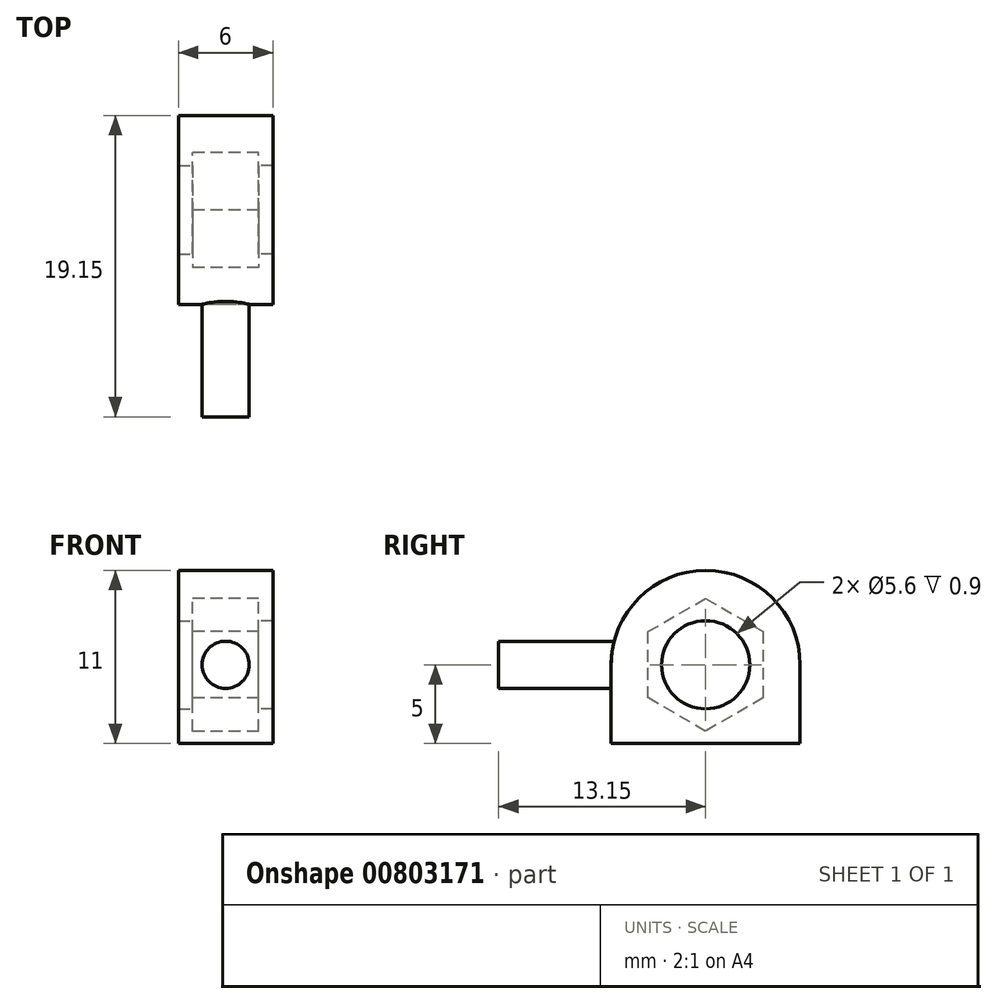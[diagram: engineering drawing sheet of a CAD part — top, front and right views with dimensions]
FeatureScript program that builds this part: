
annotation { "Feature Type Name" : "Feature", "Feature Type Description" : "" }
export const myFeature = defineFeature(function(context is Context, id is Id, definition is map)
    precondition{}
    {
        {
            var Q0;
            Q0=qCreatedBy(makeId("Right.planeOp"),FACE);
            var sketch = newSketch(context, id + "F0", { "sketchPlane" : qUnion([Q0])});
            skCircle(sketch, "E0.cCircle", {"center": v(0, 0) * mm, "radius": 3.65 * mm, "construction": true});
            skLineSegment(sketch, "E0.0", {"start": v(-3.65, 2.1) * mm, "end": v(0, 4.21) * mm});
            skLineSegment(sketch, "E0.1", {"start": v(0, 4.21) * mm, "end": v(3.65, 2.1) * mm});
            skLineSegment(sketch, "E0.2", {"start": v(3.65, 2.1) * mm, "end": v(3.65, -2.1) * mm});
            skLineSegment(sketch, "E0.3", {"start": v(3.65, -2.1) * mm, "end": v(0, -4.21) * mm});
            skLineSegment(sketch, "E0.4", {"start": v(0, -4.21) * mm, "end": v(-3.65, -2.1) * mm});
            skLineSegment(sketch, "E0.5", {"start": v(-3.65, -2.1) * mm, "end": v(-3.65, 2.1) * mm});
            skPoint(sketch, "E0.0.midPoint", {"position": v(-1.83, 3.16) * mm});
            skLineSegment(sketch, "E1", {"start": v(-11.2, -5) * mm, "end": v(14.47, -5) * mm});
            skCircle(sketch, "E2", {"center": v(0, 0) * mm, "radius": 2 * mm});
            skPoint(sketch, "E3", {"position": v(-7.15, 0) * mm});
            skPoint(sketch, "E3.positionSnap0", {"position": v(-3.65, 0) * mm});
            skPoint(sketch, "E4", {"position": v(-11.15, 0) * mm});
            skLineSegment(sketch, "E5.bottom", {"start": v(-3.65, 1.5) * mm, "end": v(-13.15, 1.5) * mm});
            skLineSegment(sketch, "E5.top", {"start": v(-3.65, -1.5) * mm, "end": v(-13.15, -1.5) * mm});
            skLineSegment(sketch, "E5.left", {"start": v(-3.65, 1.5) * mm, "end": v(-3.65, -1.5) * mm});
            skLineSegment(sketch, "E5.right", {"start": v(-13.15, 1.5) * mm, "end": v(-13.15, -1.5) * mm});
            skPoint(sketch, "E5.middle", {"position": v(-8.4, 0) * mm});
            skLineSegment(sketch, "E6", {"start": v(-6, 0) * mm, "end": v(-6, -5) * mm});
            skArc(sketch, "E7", {"start": v(-6, 0) * mm, "mid": v(-4.24, 4.24) * mm, "end": v(0, 6) * mm});
            skCircle(sketch, "E8", {"center": v(0, 0) * mm, "radius": 2.8 * mm});
            skArc(sketch, "E9.MirrorCS", {"start": v(6, 0) * mm, "mid": v(4.24, 4.24) * mm, "end": v(0, 6) * mm});
            skLineSegment(sketch, "E10.MirrorCS", {"start": v(6, 0) * mm, "end": v(6, -5) * mm});
            skLineSegment(sketch, "E11", {"start": v(-13.15, 0) * mm, "end": v(-3.65, 0) * mm});
            skSolve(sketch);
        }
        {
            var Q0;
            {var subQ8=sQuery(id+"F0.wireOp",EDGE,"E0.0");Q0=makeQuery(id+"F0.imprint","IMPRINT",FACE,{"disambiguationData":[TD([[makeQuery(id+"F0.imprint","IMPRINT",EDGE,{"derivedFrom":subQ8}),1.0]])]});}
            var Q1;
            {var subQ0=sQuery(id+"F0.wireOp",EDGE,"E5.top");var subQ1=sQuery(id+"F0.wireOp",EDGE,"E0.5");var subQ2=makeQuery(id+"F0.imprint","INTERSECT",VERTEX,{"derivedFrom":[subQ1,subQ0]});Q1=makeQuery(id+"F0.imprint","IMPRINT",FACE,{"disambiguationData":[TD([[makeQuery(id+"F0.imprint","IMPRINT",EDGE,{"disambiguationData":[TD([[subQ2,-1.0]])],"derivedFrom":subQ1}),1.0]])]});}
            var Q2;
            {var subQ0=sQuery(id+"F0.wireOp",EDGE,"E11");var subQ1=sQuery(id+"F0.wireOp",EDGE,"E0.5");var subQ2=makeQuery(id+"F0.imprint","INTERSECT",VERTEX,{"derivedFrom":[subQ1,subQ0]});Q2=makeQuery(id+"F0.imprint","IMPRINT",FACE,{"disambiguationData":[TD([[makeQuery(id+"F0.imprint","IMPRINT",EDGE,{"disambiguationData":[TD([[subQ2,-1.0]])],"derivedFrom":subQ1}),1.0]])]});}
            extrude(context, id + "F1", {"entities" : qUnion([Q0, Q1, Q2]), "endBound" : BoundingType.SYMMETRIC, "depth" : (3.2 + 1) * mm, "offsetDistance" : 25 * mm});
        }
        {
            var Q0;
            {var subQ0=sQuery(id+"F0.wireOp",EDGE,"E11");var subQ1=sQuery(id+"F0.wireOp",EDGE,"E0.5");var subQ2=makeQuery(id+"F0.imprint","INTERSECT",VERTEX,{"derivedFrom":[subQ1,subQ0]});Q0=makeQuery(id+"F0.imprint","IMPRINT",FACE,{"disambiguationData":[TD([[makeQuery(id+"F0.imprint","IMPRINT",EDGE,{"disambiguationData":[TD([[subQ2,-1.0]])],"derivedFrom":subQ1}),1.0]])]});}
            var Q1;
            {var subQ0=sQuery(id+"F0.wireOp",EDGE,"E5.top");var subQ1=sQuery(id+"F0.wireOp",EDGE,"E0.5");var subQ2=makeQuery(id+"F0.imprint","INTERSECT",VERTEX,{"derivedFrom":[subQ1,subQ0]});Q1=makeQuery(id+"F0.imprint","IMPRINT",FACE,{"disambiguationData":[TD([[makeQuery(id+"F0.imprint","IMPRINT",EDGE,{"disambiguationData":[TD([[subQ2,-1.0]])],"derivedFrom":subQ1}),1.0]])]});}
            var Q2;
            {var subQ8=sQuery(id+"F0.wireOp",EDGE,"E0.0");Q2=makeQuery(id+"F0.imprint","IMPRINT",FACE,{"disambiguationData":[TD([[makeQuery(id+"F0.imprint","IMPRINT",EDGE,{"derivedFrom":subQ8}),1.0]])]});}
            var Q3;
            {var subQ0=sQuery(id+"F0.wireOp",EDGE,"E0.0");Q3=makeQuery(id+"F0.imprint","IMPRINT",FACE,{"disambiguationData":[TD([[makeQuery(id+"F0.imprint","IMPRINT",EDGE,{"derivedFrom":subQ0}),-1.0]])]});}
            extrude(context, id + "F2", {"entities" : qUnion([Q0, Q1, Q2, Q3]), "oppositeDirection" : true, "depth" : 3 * mm, "offsetDistance" : 25 * mm, "hasSecondDirection" : true, "secondDirectionOppositeDirection" : true, "secondDirectionDepth" : (((3.2 + 1) / 2)) * mm});
        }
        {
            var Q0;
            {var subQ0=sQuery(id+"F0.wireOp",EDGE,"E7");var subQ1=sQuery(id+"F0.wireOp",EDGE,"E5.bottom");var subQ2=makeQuery(id+"F0.imprint","INTERSECT",VERTEX,{"derivedFrom":[subQ1,subQ0]});Q0=makeQuery(id+"F0.imprint","IMPRINT",FACE,{"disambiguationData":[TD([[makeQuery(id+"F0.imprint","IMPRINT",EDGE,{"disambiguationData":[TD([[subQ2,-1.0]])],"derivedFrom":subQ1}),1.0]])]});}
            var Q1;
            {var subQ0=sQuery(id+"F0.wireOp",EDGE,"E11");var subQ1=sQuery(id+"F0.wireOp",EDGE,"E0.5");var subQ2=makeQuery(id+"F0.imprint","INTERSECT",VERTEX,{"derivedFrom":[subQ1,subQ0]});Q1=makeQuery(id+"F0.imprint","IMPRINT",FACE,{"disambiguationData":[TD([[makeQuery(id+"F0.imprint","IMPRINT",EDGE,{"disambiguationData":[TD([[subQ2,-1.0]])],"derivedFrom":subQ1}),1.0]])]});}
            var Q2;
            Q2=sQuery(id+"F0.wireOp",EDGE,"E11");
            revolve(context, id + "F3", {"operationType" : NewBodyOperationType.ADD, "surfaceOperationType" : NewSurfaceOperationType.NEW, "entities" : qUnion([Q0, Q1]), "axis" : qUnion([Q2]), "revolveType" : RevolveType.FULL});
        }
        {
            var Q0;
            Q0=makeQuery(id+"F2.opExtrude","SWEPT_BODY",BODY,{"disambiguationData":[OSD([sQuery(id+"F0.wireOp",EDGE,"E1"),sQuery(id+"F0.wireOp",EDGE,"E6"),sQuery(id+"F0.wireOp",EDGE,"E7"),sQuery(id+"F0.wireOp",EDGE,"E8"),sQuery(id+"F0.wireOp",EDGE,"E9.MirrorCS"),sQuery(id+"F0.wireOp",EDGE,"E10.MirrorCS")])]});
            var Q1;
            Q1=qCreatedBy(makeId("Right.planeOp"),FACE);
            mirror(context, id + "F4", {"operationType" : NewBodyOperationType.ADD, "entities" : qUnion([Q0]), "mirrorPlane" : qUnion([Q1])});
        }
    });
